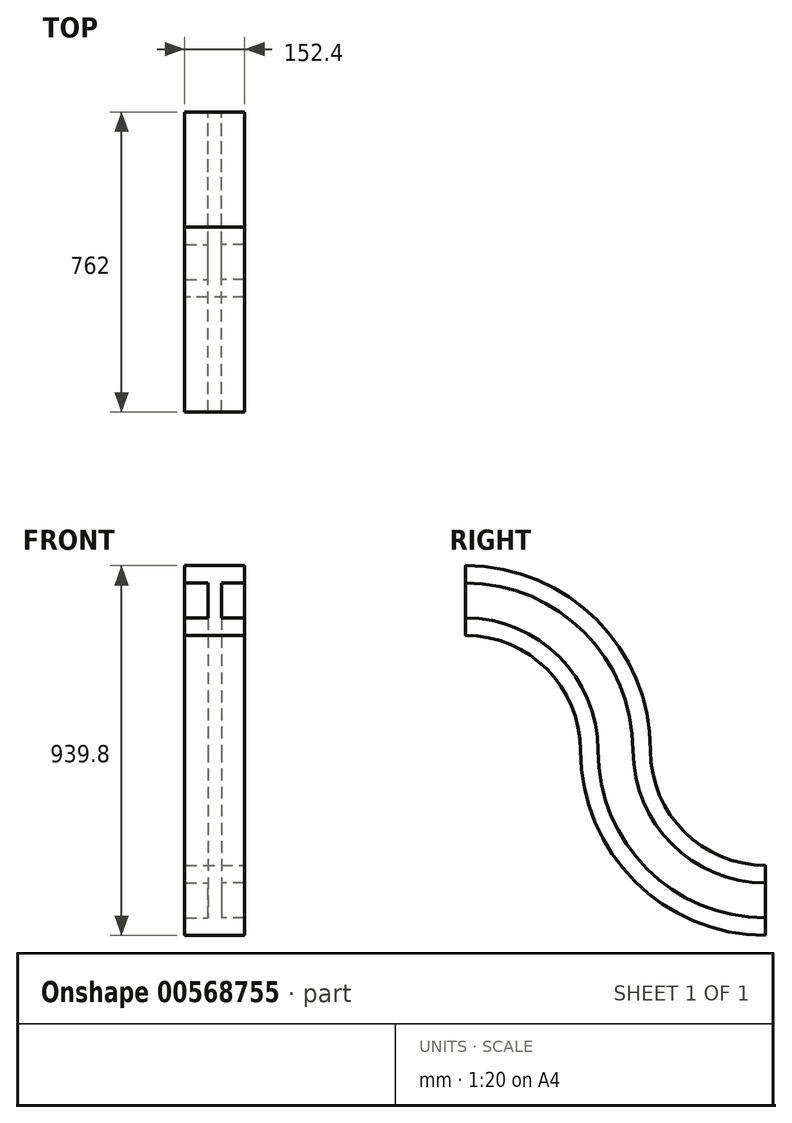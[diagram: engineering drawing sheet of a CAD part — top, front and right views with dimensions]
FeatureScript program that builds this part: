
annotation { "Feature Type Name" : "Feature", "Feature Type Description" : "" }
export const myFeature = defineFeature(function(context is Context, id is Id, definition is map)
    precondition{}
    {
        {
            var Q0;
            Q0=qCreatedBy(makeId("Front.planeOp"),FACE);
            var sketch = newSketch(context, id + "F0", { "sketchPlane" : qUnion([Q0])});
            skLineSegment(sketch, "E0", {"start": v(0, 88.9) * mm, "end": v(76.2, 88.9) * mm});
            skLineSegment(sketch, "E1", {"start": v(76.2, 88.9) * mm, "end": v(76.2, 44.45) * mm});
            skLineSegment(sketch, "E2", {"start": v(76.2, 44.45) * mm, "end": v(17.37, 44.45) * mm});
            skLineSegment(sketch, "E3", {"start": v(0, 88.9) * mm, "end": v(0, -88.9) * mm, "construction": true});
            skLineSegment(sketch, "E4", {"start": v(-17.37, 0) * mm, "end": v(17.37, 0) * mm, "construction": true});
            skLineSegment(sketch, "E5", {"start": v(17.37, 0) * mm, "end": v(17.37, 44.45) * mm});
            skLineSegment(sketch, "E6.MirrorCS", {"start": v(0, 88.9) * mm, "end": v(-76.2, 88.9) * mm});
            skLineSegment(sketch, "E7.MirrorCS", {"start": v(-76.2, 88.9) * mm, "end": v(-76.2, 44.45) * mm});
            skLineSegment(sketch, "E8.MirrorCS", {"start": v(-17.37, 0) * mm, "end": v(-17.37, 44.45) * mm});
            skLineSegment(sketch, "E9.MirrorCS", {"start": v(-76.2, 44.45) * mm, "end": v(-17.37, 44.45) * mm});
            skLineSegment(sketch, "E10.MirrorCS", {"start": v(0, -88.9) * mm, "end": v(-76.2, -88.9) * mm});
            skLineSegment(sketch, "E11.MirrorCS", {"start": v(-76.2, -88.9) * mm, "end": v(-76.2, -44.45) * mm});
            skLineSegment(sketch, "E12.MirrorCS", {"start": v(-76.2, -44.45) * mm, "end": v(-17.37, -44.45) * mm});
            skLineSegment(sketch, "E13.MirrorCS", {"start": v(-17.37, 0) * mm, "end": v(-17.37, -44.45) * mm});
            skLineSegment(sketch, "E14.MirrorCS", {"start": v(76.2, -44.45) * mm, "end": v(17.37, -44.45) * mm});
            skLineSegment(sketch, "E15.MirrorCS", {"start": v(0, -88.9) * mm, "end": v(76.2, -88.9) * mm});
            skLineSegment(sketch, "E16.MirrorCS", {"start": v(17.37, 0) * mm, "end": v(17.37, -44.45) * mm});
            skLineSegment(sketch, "E17.MirrorCS", {"start": v(76.2, -88.9) * mm, "end": v(76.2, -44.45) * mm});
            skSolve(sketch);
        }
        {
            var Q0;
            Q0=qCreatedBy(makeId("Right.planeOp"),FACE);
            var sketch = newSketch(context, id + "F1", { "sketchPlane" : qUnion([Q0])});
            skArc(sketch, "E18", {"start": v(0, 0) * mm, "mid": v(269.4, -111.6) * mm, "end": v(381, -381) * mm});
            skArc(sketch, "E19", {"start": v(381, -381) * mm, "mid": v(492.6, -650.4) * mm, "end": v(762, -762) * mm});
            skSolve(sketch);
        }
        {
            var Q0;
            Q0 = qSketchRegion(id + "F0", true);
            var Q1;
            Q1 = qConstructionFilter(qBodyType(qCreatedBy(id + "F1" ,EDGE), BodyType.WIRE), ConstructionObject.NO);
            sweep(context, id + "F2", {"profiles" : qUnion([Q0]), "path" : qUnion([Q1])});
        }
        {
            var Q0;
            Q0=makeQuery(id+"F0.imprint","IMPRINT",FACE,{"disambiguationData":[TD([[makeQuery(id+"F0.imprint","IMPRINT",EDGE,{"derivedFrom":sQuery(id+"F0.wireOp",EDGE,"E0")}),-1.0]])]});
            var Q1;
            Q1=sQuery(id+"F1.wireOp",EDGE,"E18");
            var Q2;
            Q2=sQuery(id+"F1.wireOp",EDGE,"E19");
            sweep(context, id + "F3", {"profiles" : qUnion([Q0]), "path" : qUnion([Q1, Q2])});
        }
    });
